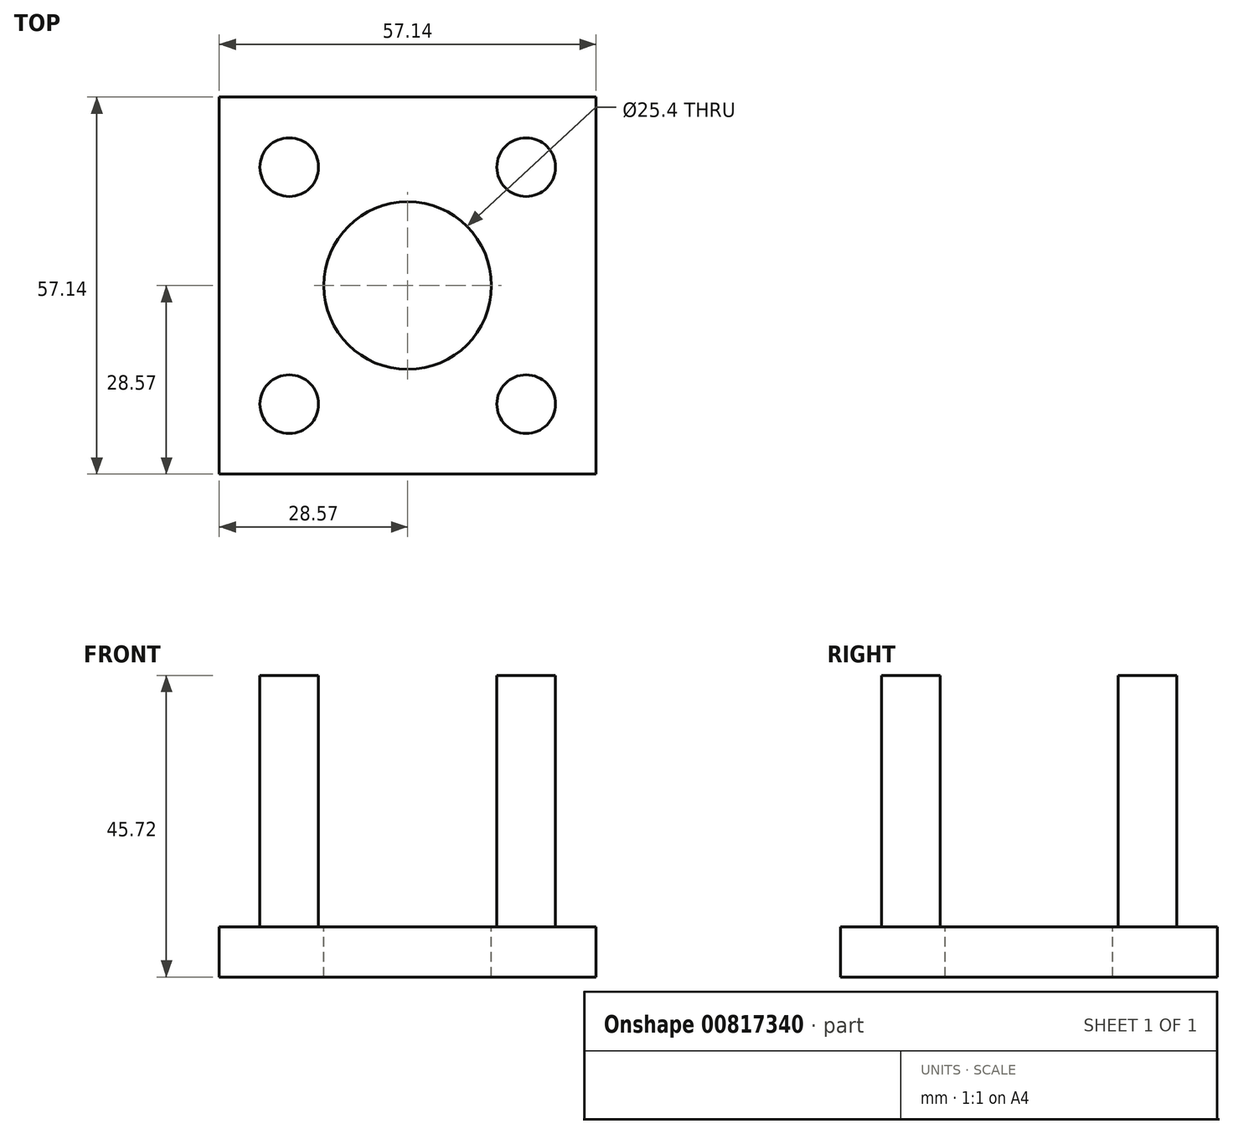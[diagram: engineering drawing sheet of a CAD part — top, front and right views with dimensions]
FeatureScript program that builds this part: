
annotation { "Feature Type Name" : "Feature", "Feature Type Description" : "" }
export const myFeature = defineFeature(function(context is Context, id is Id, definition is map)
    precondition{}
    {
        {
            var Q0;
            Q0=qCreatedBy(makeId("Top.planeOp"),FACE);
            var sketch = newSketch(context, id + "F0", { "sketchPlane" : qUnion([Q0])});
            skCircle(sketch, "E0", {"center": v(0, 0) * mm, "radius": 25.4 * mm});
            skPoint(sketch, "E1", {"position": v(17.96, 17.96) * mm});
            skPoint(sketch, "E2", {"position": v(-17.96, 17.96) * mm});
            skPoint(sketch, "E3", {"position": v(-17.96, -17.96) * mm});
            skPoint(sketch, "E4", {"position": v(17.96, -17.96) * mm});
            skLineSegment(sketch, "E5", {"start": v(-17.96, 17.96) * mm, "end": v(17.96, -17.96) * mm});
            skLineSegment(sketch, "E6", {"start": v(17.96, 17.96) * mm, "end": v(-17.96, -17.96) * mm});
            skCircle(sketch, "E7", {"center": v(17.96, 17.96) * mm, "radius": 4.45 * mm});
            skCircle(sketch, "E8", {"center": v(-17.96, 17.96) * mm, "radius": 4.45 * mm});
            skCircle(sketch, "E9", {"center": v(-17.96, -17.96) * mm, "radius": 4.45 * mm});
            skCircle(sketch, "E10", {"center": v(17.96, -17.96) * mm, "radius": 4.45 * mm});
            skCircle(sketch, "E11", {"center": v(0, 0) * mm, "radius": 12.7 * mm});
            skLineSegment(sketch, "E12.bottom", {"start": v(28.58, 28.58) * mm, "end": v(-28.58, 28.58) * mm});
            skLineSegment(sketch, "E12.top", {"start": v(28.58, -28.57) * mm, "end": v(-28.58, -28.57) * mm});
            skLineSegment(sketch, "E12.left", {"start": v(28.58, 28.58) * mm, "end": v(28.58, -28.57) * mm});
            skLineSegment(sketch, "E12.right", {"start": v(-28.58, 28.58) * mm, "end": v(-28.58, -28.57) * mm});
            skSolve(sketch);
        }
        {
            var Q0;
            {var subQ0=sQuery(id+"F0.wireOp",EDGE,"E6");var subQ1=sQuery(id+"F0.wireOp",EDGE,"E0");var subQ2=makeQuery(id+"F0.imprint","INTERSECT",VERTEX,{"disambiguationData":[OD(1.0)],"derivedFrom":[subQ1,subQ0]});Q0=makeQuery(id+"F0.imprint","IMPRINT",FACE,{"disambiguationData":[TD([[makeQuery(id+"F0.imprint","IMPRINT",EDGE,{"disambiguationData":[TD([[subQ2,-1.0]])],"derivedFrom":subQ1}),1.0]])]});}
            var Q1;
            {var subQ0=sQuery(id+"F0.wireOp",EDGE,"E6");var subQ1=sQuery(id+"F0.wireOp",EDGE,"E0");var subQ2=makeQuery(id+"F0.imprint","INTERSECT",VERTEX,{"disambiguationData":[OD(1.0)],"derivedFrom":[subQ1,subQ0]});Q1=makeQuery(id+"F0.imprint","IMPRINT",FACE,{"disambiguationData":[TD([[makeQuery(id+"F0.imprint","IMPRINT",EDGE,{"disambiguationData":[TD([[subQ2,1.0]])],"derivedFrom":subQ1}),1.0]])]});}
            var Q2;
            {var subQ0=sQuery(id+"F0.wireOp",EDGE,"E0");var subQ1=makeQuery(id+"F0.imprint","INTERSECT",VERTEX,{"disambiguationData":[OD(1.0)],"derivedFrom":[subQ0,sQuery(id+"F0.wireOp",EDGE,"E6")]});Q2=makeQuery(id+"F0.imprint","IMPRINT",FACE,{"disambiguationData":[TD([[makeQuery(id+"F0.imprint","IMPRINT",EDGE,{"disambiguationData":[TD([[subQ1,1.0]])],"derivedFrom":subQ0}),-1.0]])]});}
            var Q3;
            {var subQ0=sQuery(id+"F0.wireOp",EDGE,"E0");var subQ1=makeQuery(id+"F0.imprint","INTERSECT",VERTEX,{"disambiguationData":[OD(1.0)],"derivedFrom":[subQ0,sQuery(id+"F0.wireOp",EDGE,"E5")]});Q3=makeQuery(id+"F0.imprint","IMPRINT",FACE,{"disambiguationData":[TD([[makeQuery(id+"F0.imprint","IMPRINT",EDGE,{"disambiguationData":[TD([[subQ1,1.0]])],"derivedFrom":subQ0}),-1.0]])]});}
            var Q4;
            {var subQ0=sQuery(id+"F0.wireOp",EDGE,"E5");var subQ1=sQuery(id+"F0.wireOp",EDGE,"E0");var subQ2=makeQuery(id+"F0.imprint","INTERSECT",VERTEX,{"disambiguationData":[OD(1.0)],"derivedFrom":[subQ1,subQ0]});Q4=makeQuery(id+"F0.imprint","IMPRINT",FACE,{"disambiguationData":[TD([[makeQuery(id+"F0.imprint","IMPRINT",EDGE,{"disambiguationData":[TD([[subQ2,1.0]])],"derivedFrom":subQ1}),1.0]])]});}
            var Q5;
            {var subQ0=sQuery(id+"F0.wireOp",EDGE,"E5");var subQ1=sQuery(id+"F0.wireOp",EDGE,"E0");var subQ2=makeQuery(id+"F0.imprint","INTERSECT",VERTEX,{"disambiguationData":[OD(1.0)],"derivedFrom":[subQ1,subQ0]});Q5=makeQuery(id+"F0.imprint","IMPRINT",FACE,{"disambiguationData":[TD([[makeQuery(id+"F0.imprint","IMPRINT",EDGE,{"disambiguationData":[TD([[subQ2,-1.0]])],"derivedFrom":subQ1}),1.0]])]});}
            var Q6;
            {var subQ0=sQuery(id+"F0.wireOp",EDGE,"E6");var subQ1=sQuery(id+"F0.wireOp",EDGE,"E0");var subQ2=makeQuery(id+"F0.imprint","INTERSECT",VERTEX,{"disambiguationData":[OD(0.0)],"derivedFrom":[subQ1,subQ0]});Q6=makeQuery(id+"F0.imprint","IMPRINT",FACE,{"disambiguationData":[TD([[makeQuery(id+"F0.imprint","IMPRINT",EDGE,{"disambiguationData":[TD([[subQ2,1.0]])],"derivedFrom":subQ1}),1.0]])]});}
            var Q7;
            {var subQ0=sQuery(id+"F0.wireOp",EDGE,"E0");var subQ1=makeQuery(id+"F0.imprint","INTERSECT",VERTEX,{"disambiguationData":[OD(0.0)],"derivedFrom":[subQ0,sQuery(id+"F0.wireOp",EDGE,"E6")]});Q7=makeQuery(id+"F0.imprint","IMPRINT",FACE,{"disambiguationData":[TD([[makeQuery(id+"F0.imprint","IMPRINT",EDGE,{"disambiguationData":[TD([[subQ1,1.0]])],"derivedFrom":subQ0}),-1.0]])]});}
            var Q8;
            {var subQ0=sQuery(id+"F0.wireOp",EDGE,"E6");var subQ1=sQuery(id+"F0.wireOp",EDGE,"E0");var subQ2=makeQuery(id+"F0.imprint","INTERSECT",VERTEX,{"disambiguationData":[OD(0.0)],"derivedFrom":[subQ1,subQ0]});Q8=makeQuery(id+"F0.imprint","IMPRINT",FACE,{"disambiguationData":[TD([[makeQuery(id+"F0.imprint","IMPRINT",EDGE,{"disambiguationData":[TD([[subQ2,-1.0]])],"derivedFrom":subQ1}),1.0]])]});}
            var Q9;
            {var subQ0=sQuery(id+"F0.wireOp",EDGE,"E5");var subQ1=sQuery(id+"F0.wireOp",EDGE,"E0");var subQ2=makeQuery(id+"F0.imprint","INTERSECT",VERTEX,{"disambiguationData":[OD(0.0)],"derivedFrom":[subQ1,subQ0]});Q9=makeQuery(id+"F0.imprint","IMPRINT",FACE,{"disambiguationData":[TD([[makeQuery(id+"F0.imprint","IMPRINT",EDGE,{"disambiguationData":[TD([[subQ2,1.0]])],"derivedFrom":subQ1}),1.0]])]});}
            var Q10;
            {var subQ0=sQuery(id+"F0.wireOp",EDGE,"E5");var subQ1=sQuery(id+"F0.wireOp",EDGE,"E0");var subQ2=makeQuery(id+"F0.imprint","INTERSECT",VERTEX,{"disambiguationData":[OD(0.0)],"derivedFrom":[subQ1,subQ0]});Q10=makeQuery(id+"F0.imprint","IMPRINT",FACE,{"disambiguationData":[TD([[makeQuery(id+"F0.imprint","IMPRINT",EDGE,{"disambiguationData":[TD([[subQ2,-1.0]])],"derivedFrom":subQ1}),1.0]])]});}
            var Q11;
            {var subQ0=sQuery(id+"F0.wireOp",EDGE,"E0");var subQ1=makeQuery(id+"F0.imprint","INTERSECT",VERTEX,{"disambiguationData":[OD(0.0)],"derivedFrom":[subQ0,sQuery(id+"F0.wireOp",EDGE,"E5")]});Q11=makeQuery(id+"F0.imprint","IMPRINT",FACE,{"disambiguationData":[TD([[makeQuery(id+"F0.imprint","IMPRINT",EDGE,{"disambiguationData":[TD([[subQ1,1.0]])],"derivedFrom":subQ0}),-1.0]])]});}
            var Q12;
            {var subQ5=sQuery(id+"F0.wireOp",EDGE,"E8");var subQ6=sQuery(id+"F0.wireOp",EDGE,"E0");var subQ7=makeQuery(id+"F0.imprint","INTERSECT",VERTEX,{"disambiguationData":[OD(1.0)],"derivedFrom":[subQ6,subQ5]});Q12=makeQuery(id+"F0.imprint","IMPRINT",FACE,{"disambiguationData":[TD([[makeQuery(id+"F0.imprint","IMPRINT",EDGE,{"disambiguationData":[TD([[subQ7,-1.0]])],"derivedFrom":subQ6}),1.0]])]});}
            var Q13;
            Q13=makeQuery(id+"F0.imprint","IMPRINT",FACE,{"disambiguationData":[TD([[makeQuery(id+"F0.imprint","IMPRINT",EDGE,{"derivedFrom":sQuery(id+"F0.wireOp",EDGE,"E12.bottom")}),1.0]])]});
            var Q14;
            {var subQ0=sQuery(id+"F0.wireOp",EDGE,"E9");var subQ1=sQuery(id+"F0.wireOp",EDGE,"E0");var subQ2=makeQuery(id+"F0.imprint","INTERSECT",VERTEX,{"disambiguationData":[OD(1.0)],"derivedFrom":[subQ1,subQ0]});Q14=makeQuery(id+"F0.imprint","IMPRINT",FACE,{"disambiguationData":[TD([[makeQuery(id+"F0.imprint","IMPRINT",EDGE,{"disambiguationData":[TD([[subQ2,-1.0]])],"derivedFrom":subQ1}),1.0]])]});}
            var Q15;
            {var subQ0=sQuery(id+"F0.wireOp",EDGE,"E7");var subQ1=sQuery(id+"F0.wireOp",EDGE,"E0");var subQ2=makeQuery(id+"F0.imprint","INTERSECT",VERTEX,{"disambiguationData":[OD(0.0)],"derivedFrom":[subQ1,subQ0]});Q15=makeQuery(id+"F0.imprint","IMPRINT",FACE,{"disambiguationData":[TD([[makeQuery(id+"F0.imprint","IMPRINT",EDGE,{"disambiguationData":[TD([[subQ2,1.0]])],"derivedFrom":subQ1}),1.0]])]});}
            var Q16;
            {var subQ0=sQuery(id+"F0.wireOp",EDGE,"E7");var subQ1=sQuery(id+"F0.wireOp",EDGE,"E0");var subQ2=makeQuery(id+"F0.imprint","INTERSECT",VERTEX,{"disambiguationData":[OD(1.0)],"derivedFrom":[subQ1,subQ0]});Q16=makeQuery(id+"F0.imprint","IMPRINT",FACE,{"disambiguationData":[TD([[makeQuery(id+"F0.imprint","IMPRINT",EDGE,{"disambiguationData":[TD([[subQ2,-1.0]])],"derivedFrom":subQ1}),1.0]])]});}
            var Q17;
            {var subQ0=sQuery(id+"F0.wireOp",EDGE,"E11");var subQ1=sQuery(id+"F0.wireOp",EDGE,"E5");var subQ2=makeQuery(id+"F0.imprint","INTERSECT",VERTEX,{"disambiguationData":[OD(0.0)],"derivedFrom":[subQ1,subQ0]});Q17=makeQuery(id+"F0.imprint","IMPRINT",FACE,{"disambiguationData":[TD([[makeQuery(id+"F0.imprint","IMPRINT",EDGE,{"disambiguationData":[TD([[subQ2,-1.0]])],"derivedFrom":subQ1}),1.0]])]});}
            var Q18;
            {var subQ0=sQuery(id+"F0.wireOp",EDGE,"E6");var subQ1=sQuery(id+"F0.wireOp",EDGE,"E5");var subQ2=makeQuery(id+"F0.imprint","INTERSECT",VERTEX,{"derivedFrom":[subQ1,subQ0]});Q18=makeQuery(id+"F0.imprint","IMPRINT",FACE,{"disambiguationData":[TD([[makeQuery(id+"F0.imprint","IMPRINT",EDGE,{"disambiguationData":[TD([[subQ2,-1.0]])],"derivedFrom":subQ1}),1.0]])]});}
            var Q19;
            {var subQ0=sQuery(id+"F0.wireOp",EDGE,"E6");var subQ1=sQuery(id+"F0.wireOp",EDGE,"E5");var subQ2=makeQuery(id+"F0.imprint","INTERSECT",VERTEX,{"derivedFrom":[subQ1,subQ0]});Q19=makeQuery(id+"F0.imprint","IMPRINT",FACE,{"disambiguationData":[TD([[makeQuery(id+"F0.imprint","IMPRINT",EDGE,{"disambiguationData":[TD([[subQ2,-1.0]])],"derivedFrom":subQ1}),-1.0]])]});}
            var Q20;
            {var subQ0=sQuery(id+"F0.wireOp",EDGE,"E11");var subQ1=sQuery(id+"F0.wireOp",EDGE,"E5");var subQ2=makeQuery(id+"F0.imprint","INTERSECT",VERTEX,{"disambiguationData":[OD(0.0)],"derivedFrom":[subQ1,subQ0]});Q20=makeQuery(id+"F0.imprint","IMPRINT",FACE,{"disambiguationData":[TD([[makeQuery(id+"F0.imprint","IMPRINT",EDGE,{"disambiguationData":[TD([[subQ2,-1.0]])],"derivedFrom":subQ1}),-1.0]])]});}
            extrude(context, id + "F1", {"entities" : qUnion([Q0, Q1, Q2, Q3, Q4, Q5, Q6, Q7, Q8, Q9, Q10, Q11, Q12, Q13, Q14, Q15, Q16, Q17, Q18, Q19, Q20]), "oppositeDirection" : true, "depth" : 7.62 * mm, "offsetDistance" : 25.4 * mm});
        }
        {
            var Q0;
            {var subQ0=sQuery(id+"F0.wireOp",EDGE,"E6");var subQ1=sQuery(id+"F0.wireOp",EDGE,"E5");var subQ2=makeQuery(id+"F0.imprint","INTERSECT",VERTEX,{"derivedFrom":[subQ1,subQ0]});Q0=makeQuery(id+"F0.imprint","IMPRINT",FACE,{"disambiguationData":[TD([[makeQuery(id+"F0.imprint","IMPRINT",EDGE,{"disambiguationData":[TD([[subQ2,-1.0]])],"derivedFrom":subQ1}),-1.0]])]});}
            var Q1;
            {var subQ0=sQuery(id+"F0.wireOp",EDGE,"E6");var subQ1=sQuery(id+"F0.wireOp",EDGE,"E5");var subQ2=makeQuery(id+"F0.imprint","INTERSECT",VERTEX,{"derivedFrom":[subQ1,subQ0]});Q1=makeQuery(id+"F0.imprint","IMPRINT",FACE,{"disambiguationData":[TD([[makeQuery(id+"F0.imprint","IMPRINT",EDGE,{"disambiguationData":[TD([[subQ2,-1.0]])],"derivedFrom":subQ1}),1.0]])]});}
            var Q2;
            {var subQ0=sQuery(id+"F0.wireOp",EDGE,"E11");var subQ1=sQuery(id+"F0.wireOp",EDGE,"E5");var subQ2=makeQuery(id+"F0.imprint","INTERSECT",VERTEX,{"disambiguationData":[OD(0.0)],"derivedFrom":[subQ1,subQ0]});Q2=makeQuery(id+"F0.imprint","IMPRINT",FACE,{"disambiguationData":[TD([[makeQuery(id+"F0.imprint","IMPRINT",EDGE,{"disambiguationData":[TD([[subQ2,-1.0]])],"derivedFrom":subQ1}),1.0]])]});}
            var Q3;
            {var subQ0=sQuery(id+"F0.wireOp",EDGE,"E11");var subQ1=sQuery(id+"F0.wireOp",EDGE,"E5");var subQ2=makeQuery(id+"F0.imprint","INTERSECT",VERTEX,{"disambiguationData":[OD(0.0)],"derivedFrom":[subQ1,subQ0]});Q3=makeQuery(id+"F0.imprint","IMPRINT",FACE,{"disambiguationData":[TD([[makeQuery(id+"F0.imprint","IMPRINT",EDGE,{"disambiguationData":[TD([[subQ2,-1.0]])],"derivedFrom":subQ1}),-1.0]])]});}
            extrude(context, id + "F2", {"entities" : qUnion([Q0, Q1, Q2, Q3]), "operationType" : NewBodyOperationType.REMOVE, "depth" : -7.62 * mm, "offsetDistance" : 25.4 * mm});
        }
        {
            var Q0;
            {var subQ0=sQuery(id+"F0.wireOp",EDGE,"E0");var subQ1=makeQuery(id+"F0.imprint","INTERSECT",VERTEX,{"disambiguationData":[OD(1.0)],"derivedFrom":[subQ0,sQuery(id+"F0.wireOp",EDGE,"E6")]});Q0=makeQuery(id+"F0.imprint","IMPRINT",FACE,{"disambiguationData":[TD([[makeQuery(id+"F0.imprint","IMPRINT",EDGE,{"disambiguationData":[TD([[subQ1,1.0]])],"derivedFrom":subQ0}),-1.0]])]});}
            var Q1;
            {var subQ0=sQuery(id+"F0.wireOp",EDGE,"E6");var subQ1=sQuery(id+"F0.wireOp",EDGE,"E0");var subQ2=makeQuery(id+"F0.imprint","INTERSECT",VERTEX,{"disambiguationData":[OD(1.0)],"derivedFrom":[subQ1,subQ0]});Q1=makeQuery(id+"F0.imprint","IMPRINT",FACE,{"disambiguationData":[TD([[makeQuery(id+"F0.imprint","IMPRINT",EDGE,{"disambiguationData":[TD([[subQ2,1.0]])],"derivedFrom":subQ1}),1.0]])]});}
            var Q2;
            {var subQ0=sQuery(id+"F0.wireOp",EDGE,"E6");var subQ1=sQuery(id+"F0.wireOp",EDGE,"E0");var subQ2=makeQuery(id+"F0.imprint","INTERSECT",VERTEX,{"disambiguationData":[OD(1.0)],"derivedFrom":[subQ1,subQ0]});Q2=makeQuery(id+"F0.imprint","IMPRINT",FACE,{"disambiguationData":[TD([[makeQuery(id+"F0.imprint","IMPRINT",EDGE,{"disambiguationData":[TD([[subQ2,-1.0]])],"derivedFrom":subQ1}),1.0]])]});}
            var Q3;
            {var subQ0=sQuery(id+"F0.wireOp",EDGE,"E5");var subQ1=sQuery(id+"F0.wireOp",EDGE,"E0");var subQ2=makeQuery(id+"F0.imprint","INTERSECT",VERTEX,{"disambiguationData":[OD(1.0)],"derivedFrom":[subQ1,subQ0]});Q3=makeQuery(id+"F0.imprint","IMPRINT",FACE,{"disambiguationData":[TD([[makeQuery(id+"F0.imprint","IMPRINT",EDGE,{"disambiguationData":[TD([[subQ2,1.0]])],"derivedFrom":subQ1}),1.0]])]});}
            var Q4;
            {var subQ0=sQuery(id+"F0.wireOp",EDGE,"E5");var subQ1=sQuery(id+"F0.wireOp",EDGE,"E0");var subQ2=makeQuery(id+"F0.imprint","INTERSECT",VERTEX,{"disambiguationData":[OD(1.0)],"derivedFrom":[subQ1,subQ0]});Q4=makeQuery(id+"F0.imprint","IMPRINT",FACE,{"disambiguationData":[TD([[makeQuery(id+"F0.imprint","IMPRINT",EDGE,{"disambiguationData":[TD([[subQ2,-1.0]])],"derivedFrom":subQ1}),1.0]])]});}
            var Q5;
            {var subQ0=sQuery(id+"F0.wireOp",EDGE,"E0");var subQ1=makeQuery(id+"F0.imprint","INTERSECT",VERTEX,{"disambiguationData":[OD(1.0)],"derivedFrom":[subQ0,sQuery(id+"F0.wireOp",EDGE,"E5")]});Q5=makeQuery(id+"F0.imprint","IMPRINT",FACE,{"disambiguationData":[TD([[makeQuery(id+"F0.imprint","IMPRINT",EDGE,{"disambiguationData":[TD([[subQ1,1.0]])],"derivedFrom":subQ0}),-1.0]])]});}
            var Q6;
            {var subQ0=sQuery(id+"F0.wireOp",EDGE,"E0");var subQ1=makeQuery(id+"F0.imprint","INTERSECT",VERTEX,{"disambiguationData":[OD(0.0)],"derivedFrom":[subQ0,sQuery(id+"F0.wireOp",EDGE,"E6")]});Q6=makeQuery(id+"F0.imprint","IMPRINT",FACE,{"disambiguationData":[TD([[makeQuery(id+"F0.imprint","IMPRINT",EDGE,{"disambiguationData":[TD([[subQ1,1.0]])],"derivedFrom":subQ0}),-1.0]])]});}
            var Q7;
            {var subQ0=sQuery(id+"F0.wireOp",EDGE,"E6");var subQ1=sQuery(id+"F0.wireOp",EDGE,"E0");var subQ2=makeQuery(id+"F0.imprint","INTERSECT",VERTEX,{"disambiguationData":[OD(0.0)],"derivedFrom":[subQ1,subQ0]});Q7=makeQuery(id+"F0.imprint","IMPRINT",FACE,{"disambiguationData":[TD([[makeQuery(id+"F0.imprint","IMPRINT",EDGE,{"disambiguationData":[TD([[subQ2,1.0]])],"derivedFrom":subQ1}),1.0]])]});}
            var Q8;
            {var subQ0=sQuery(id+"F0.wireOp",EDGE,"E6");var subQ1=sQuery(id+"F0.wireOp",EDGE,"E0");var subQ2=makeQuery(id+"F0.imprint","INTERSECT",VERTEX,{"disambiguationData":[OD(0.0)],"derivedFrom":[subQ1,subQ0]});Q8=makeQuery(id+"F0.imprint","IMPRINT",FACE,{"disambiguationData":[TD([[makeQuery(id+"F0.imprint","IMPRINT",EDGE,{"disambiguationData":[TD([[subQ2,-1.0]])],"derivedFrom":subQ1}),1.0]])]});}
            var Q9;
            {var subQ0=sQuery(id+"F0.wireOp",EDGE,"E0");var subQ1=makeQuery(id+"F0.imprint","INTERSECT",VERTEX,{"disambiguationData":[OD(0.0)],"derivedFrom":[subQ0,sQuery(id+"F0.wireOp",EDGE,"E5")]});Q9=makeQuery(id+"F0.imprint","IMPRINT",FACE,{"disambiguationData":[TD([[makeQuery(id+"F0.imprint","IMPRINT",EDGE,{"disambiguationData":[TD([[subQ1,1.0]])],"derivedFrom":subQ0}),-1.0]])]});}
            var Q10;
            {var subQ0=sQuery(id+"F0.wireOp",EDGE,"E5");var subQ1=sQuery(id+"F0.wireOp",EDGE,"E0");var subQ2=makeQuery(id+"F0.imprint","INTERSECT",VERTEX,{"disambiguationData":[OD(0.0)],"derivedFrom":[subQ1,subQ0]});Q10=makeQuery(id+"F0.imprint","IMPRINT",FACE,{"disambiguationData":[TD([[makeQuery(id+"F0.imprint","IMPRINT",EDGE,{"disambiguationData":[TD([[subQ2,1.0]])],"derivedFrom":subQ1}),1.0]])]});}
            var Q11;
            {var subQ0=sQuery(id+"F0.wireOp",EDGE,"E5");var subQ1=sQuery(id+"F0.wireOp",EDGE,"E0");var subQ2=makeQuery(id+"F0.imprint","INTERSECT",VERTEX,{"disambiguationData":[OD(0.0)],"derivedFrom":[subQ1,subQ0]});Q11=makeQuery(id+"F0.imprint","IMPRINT",FACE,{"disambiguationData":[TD([[makeQuery(id+"F0.imprint","IMPRINT",EDGE,{"disambiguationData":[TD([[subQ2,-1.0]])],"derivedFrom":subQ1}),1.0]])]});}
            extrude(context, id + "F3", {"entities" : qUnion([Q0, Q1, Q2, Q3, Q4, Q5, Q6, Q7, Q8, Q9, Q10, Q11]), "operationType" : NewBodyOperationType.ADD, "depth" : 38.1 * mm, "offsetDistance" : 25.4 * mm});
        }
    });
